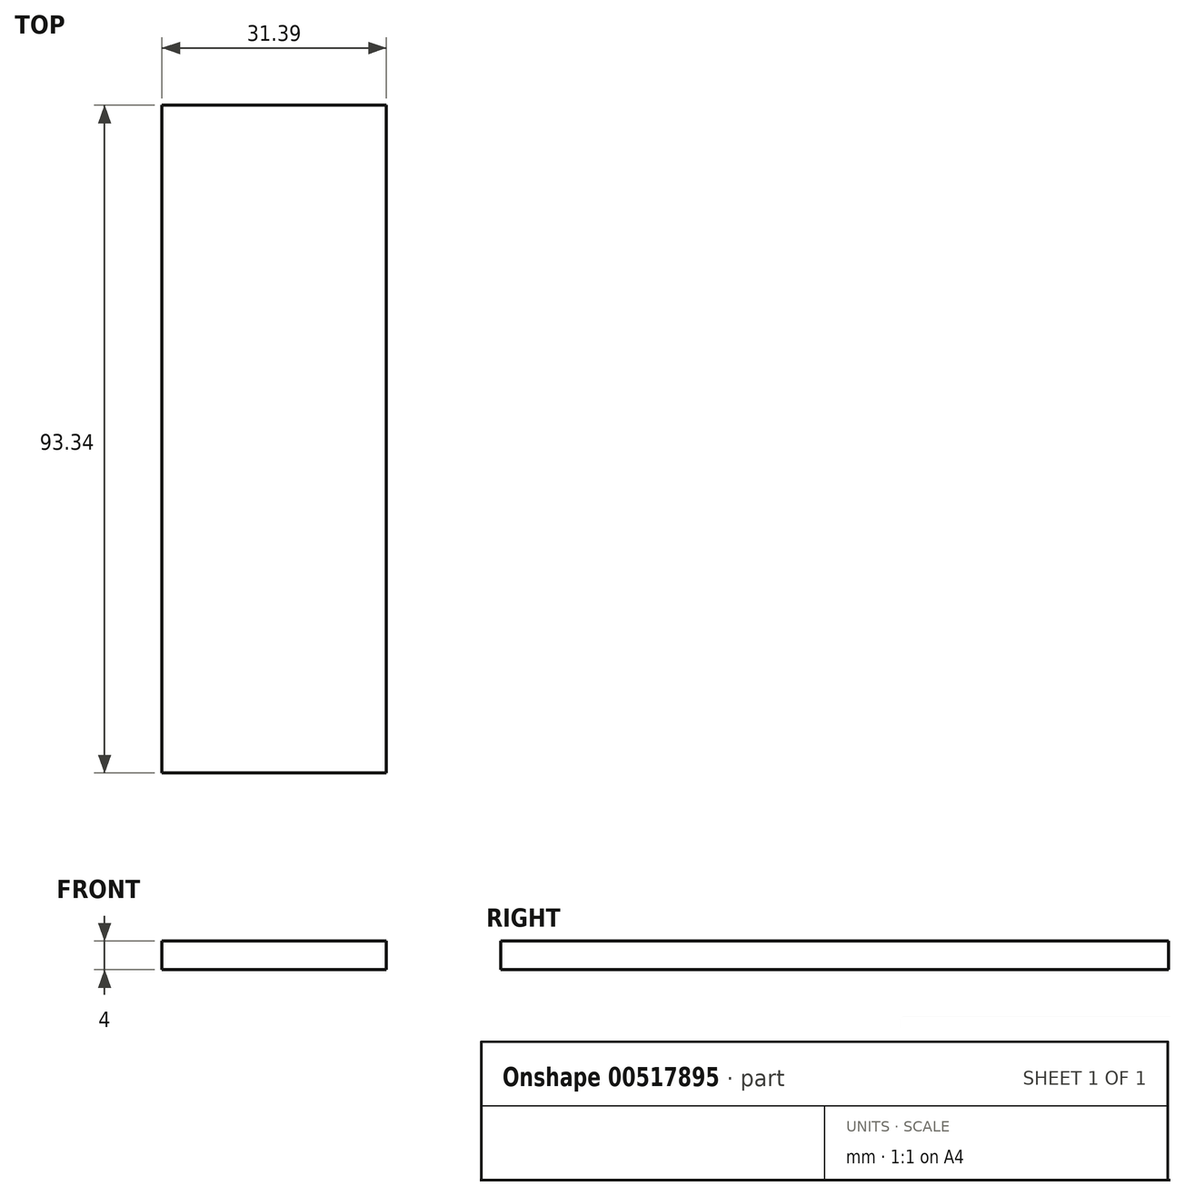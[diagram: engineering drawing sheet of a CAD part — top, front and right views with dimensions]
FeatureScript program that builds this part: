
annotation { "Feature Type Name" : "Feature", "Feature Type Description" : "" }
export const myFeature = defineFeature(function(context is Context, id is Id, definition is map)
    precondition{}
    {
        {
            var Q0;
            Q0=qCreatedBy(makeId("Top.planeOp"),FACE);
            var sketch = newSketch(context, id + "F0", { "sketchPlane" : qUnion([Q0])});
            skLineSegment(sketch, "E0.bottom", {"start": v(9.35, -31.97) * mm, "end": v(40.74, -31.97) * mm});
            skLineSegment(sketch, "E0.top", {"start": v(9.35, 61.37) * mm, "end": v(40.74, 61.37) * mm});
            skLineSegment(sketch, "E0.left", {"start": v(9.35, -31.97) * mm, "end": v(9.35, 61.37) * mm});
            skLineSegment(sketch, "E0.right", {"start": v(40.74, -31.97) * mm, "end": v(40.74, 61.37) * mm});
            skSolve(sketch);
        }
        {
            var Q0;
            Q0 = qSketchRegion(id + "F0", true);
            extrude(context, id + "F1", {"entities" : qUnion([Q0]), "depth" : 4 * mm, "offsetDistance" : 25.4 * mm});
        }
        {
            var Q0;
            Q0=makeQuery(id+"F1.opExtrude","CAP_FACE",FACE,{"disambiguationData":[OSD([sQuery(id+"F0.wireOp",EDGE,"E0.bottom"),sQuery(id+"F0.wireOp",EDGE,"E0.top"),sQuery(id+"F0.wireOp",EDGE,"E0.left"),sQuery(id+"F0.wireOp",EDGE,"E0.right")])],"isStart":false});
            var sketch = newSketch(context, id + "F2", { "sketchPlane" : qUnion([Q0])});
            skLineSegment(sketch, "E1", {"start": v(25.05, 61.37) * mm, "end": v(25.05, -31.97) * mm});
            skLineSegment(sketch, "E2", {"start": v(40.74, 14.7) * mm, "end": v(9.35, 14.7) * mm});
            skCircle(sketch, "E3", {"center": v(25.05, 14.7) * mm, "radius": 6.1 * mm});
            skLineSegment(sketch, "E4", {"start": v(40.74, 40.11) * mm, "end": v(9.35, 40.11) * mm});
            skLineSegment(sketch, "E5", {"start": v(40.74, -8.84) * mm, "end": v(9.35, -8.84) * mm});
            skSolve(sketch);
        }
        {
            var Q0;
            Q0=sQuery(id+"F2.wireOp",EDGE,"E3");
            extrude(context, id + "F3", {"bodyType" : ToolBodyType.SURFACE, "surfaceEntities" : qUnion([Q0]), "oppositeDirection" : true, "depth" : 4 * mm, "offsetDistance" : 25 * mm});
        }
    });
